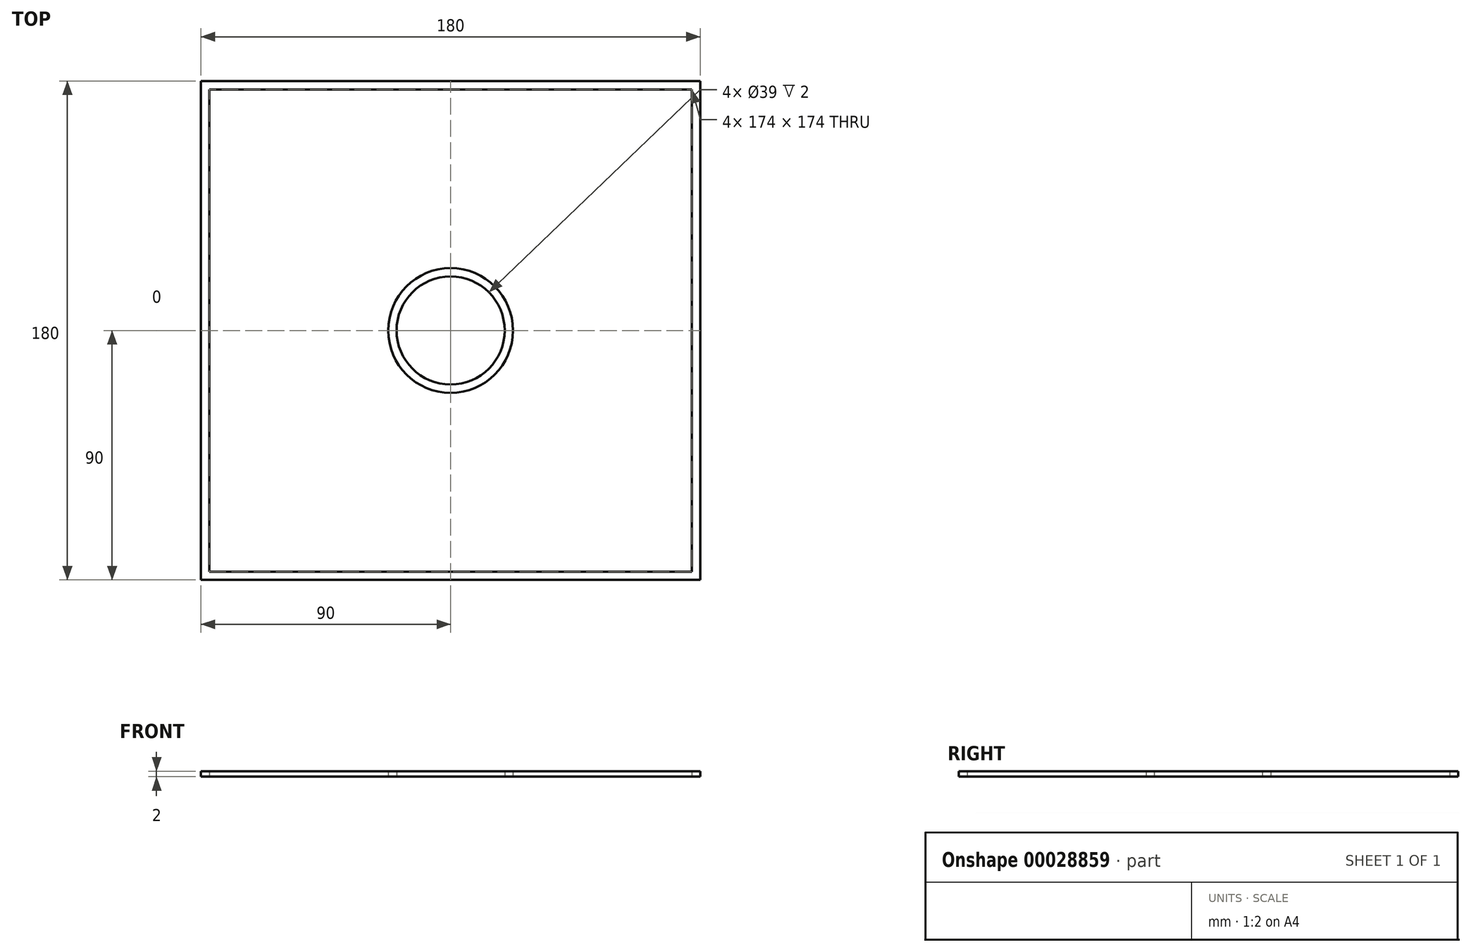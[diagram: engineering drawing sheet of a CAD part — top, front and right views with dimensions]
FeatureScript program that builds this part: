
annotation { "Feature Type Name" : "Feature", "Feature Type Description" : "" }
export const myFeature = defineFeature(function(context is Context, id is Id, definition is map)
    precondition{}
    {
        {
            var Q0;
            Q0=qCreatedBy(makeId("Top.planeOp"),FACE);
            var sketch = newSketch(context, id + "F0", { "sketchPlane" : qUnion([Q0])});
            skLineSegment(sketch, "E0.bottom", {"start": v(0, 0) * mm, "end": v(180, 0) * mm});
            skLineSegment(sketch, "E0.top", {"start": v(0, -180) * mm, "end": v(180, -180) * mm});
            skLineSegment(sketch, "E0.left", {"start": v(0, 0) * mm, "end": v(0, -180) * mm});
            skLineSegment(sketch, "E0.right", {"start": v(180, 0) * mm, "end": v(180, -180) * mm});
            skLineSegment(sketch, "E1.0", {"start": v(3, -3) * mm, "end": v(177, -3) * mm});
            skLineSegment(sketch, "E2.0", {"start": v(177, -3) * mm, "end": v(177, -177) * mm});
            skLineSegment(sketch, "E3.0", {"start": v(3, -177) * mm, "end": v(177, -177) * mm});
            skLineSegment(sketch, "E4.0", {"start": v(3, -3) * mm, "end": v(3, -177) * mm});
            skLineSegment(sketch, "E5", {"start": v(3, -90) * mm, "end": v(177, -90) * mm, "construction": true});
            skLineSegment(sketch, "E6", {"start": v(90, -3) * mm, "end": v(90, -177) * mm, "construction": true});
            skCircle(sketch, "E7", {"center": v(90, -90) * mm, "radius": 22.5 * mm});
            skCircle(sketch, "E8.0", {"center": v(90, -90) * mm, "radius": 19.5 * mm});
            skSolve(sketch);
        }
        {
            var Q0;
            Q0=makeQuery(id+"F0.imprint","IMPRINT",FACE,{"disambiguationData":[TD([[makeQuery(id+"F0.imprint","IMPRINT",EDGE,{"derivedFrom":sQuery(id+"F0.wireOp",EDGE,"E0.bottom")}),-1.0]])]});
            var Q1;
            Q1=makeQuery(id+"F0.imprint","IMPRINT",FACE,{"disambiguationData":[TD([[makeQuery(id+"F0.imprint","IMPRINT",EDGE,{"derivedFrom":sQuery(id+"F0.wireOp",EDGE,"E7")}),1.0]])]});
            extrude(context, id + "F1", {"entities" : qUnion([Q0, Q1]), "depth" : 2 * mm});
        }
    });
